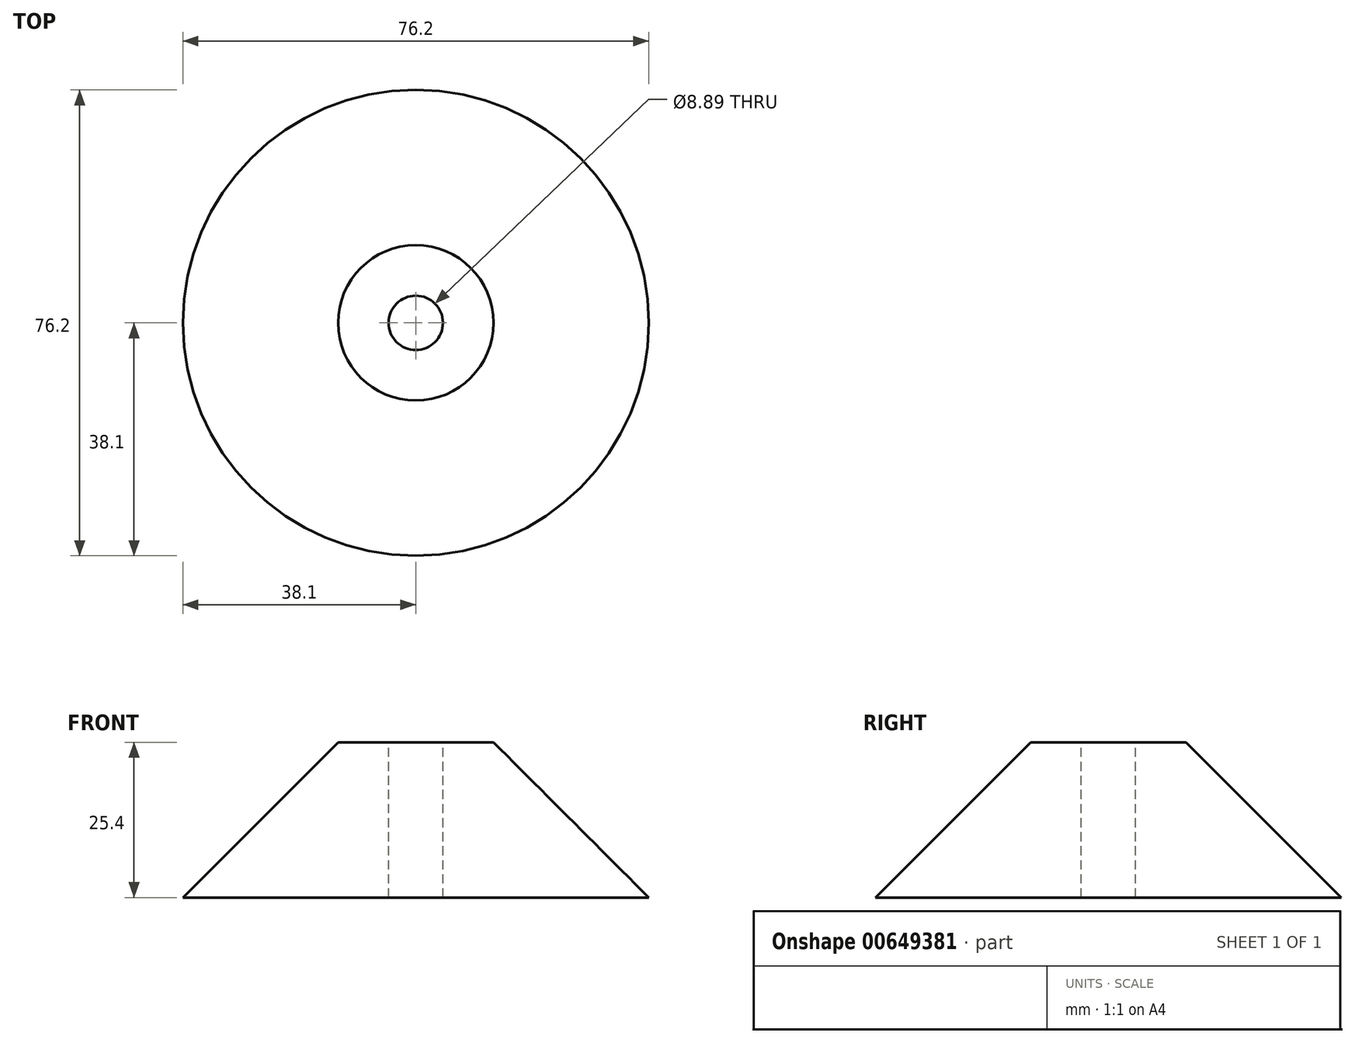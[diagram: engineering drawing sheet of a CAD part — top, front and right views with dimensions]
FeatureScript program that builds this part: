
annotation { "Feature Type Name" : "Feature", "Feature Type Description" : "" }
export const myFeature = defineFeature(function(context is Context, id is Id, definition is map)
    precondition{}
    {
        {
            var Q0;
            Q0=qCreatedBy(makeId("Top.planeOp"),FACE);
            var sketch = newSketch(context, id + "F0", { "sketchPlane" : qUnion([Q0])});
            skCircle(sketch, "E0", {"center": v(0, 0) * mm, "radius": 38.1 * mm});
            skSolve(sketch);
        }
        {
            var Q0;
            Q0=qCreatedBy(makeId("Top.planeOp"),FACE);
            cPlane(context, id + "F1", {"entities" : qUnion([Q0]), "cplaneType" : CPlaneType.OFFSET, "offset" : 25.4 * mm, "width" : 152.4 * mm, "height" : 152.4 * mm});
        }
        {
            var Q0;
            Q0=qCreatedBy(id+"F1.planeOp",FACE);
            var sketch = newSketch(context, id + "F2", { "sketchPlane" : qUnion([Q0])});
            skCircle(sketch, "E1", {"center": v(0, 0) * mm, "radius": 12.7 * mm});
            skSolve(sketch);
        }
        {
            var Q0;
            Q0=makeQuery(id+"F0.imprint","IMPRINT",FACE,{"disambiguationData":[TD([[makeQuery(id+"F0.imprint","IMPRINT",EDGE,{"derivedFrom":sQuery(id+"F0.wireOp",EDGE,"E0")}),1.0]])]});
            var Q1;
            Q1=makeQuery(id+"F2.imprint","IMPRINT",FACE,{"disambiguationData":[TD([[makeQuery(id+"F2.imprint","IMPRINT",EDGE,{"derivedFrom":sQuery(id+"F2.wireOp",EDGE,"E1")}),1.0]])]});
            var Q2;
            Q2=sQuery(id+"F2.wireOp",EDGE,"E1");
            loft(context, id + "F3", {"startCondition" : LoftEndDerivativeType.NORMAL_TO_PROFILE, "startMagnitude" : 0, "sheetProfilesArray" : [{ "sheetProfileEntities" : qUnion([Q0]) }, { "sheetProfileEntities" : qUnion([Q1]) }], "guidesArray" : [{ "guideEntities" : qUnion([Q2]), "guideDerivativeType" : LoftGuideDerivativeType.DEFAULT, "guideDerivativeMagnitude" : 1 }]});
        }
        {
            var Q0;
            Q0=makeQuery(id+"F3.opLoft","CAP_FACE",FACE,{"disambiguationData":[OSD([makeQuery(id+"F2.imprint","IMPRINT",FACE,{"disambiguationData":[TD([[makeQuery(id+"F2.imprint","IMPRINT",EDGE,{"derivedFrom":sQuery(id+"F2.wireOp",EDGE,"E1")}),1.0]])]})])],"isStart":true});
            var sketch = newSketch(context, id + "F4", { "sketchPlane" : qUnion([Q0])});
            skPoint(sketch, "E2", {"position": v(0, 0) * mm});
            skSolve(sketch);
        }
        {
            var Q0;
            Q0=sQuery(id+"F4.wireOp",VERTEX,"E2");
            var Q1;
            Q1=makeQuery(id+"F3.opLoft","SWEPT_BODY",BODY,{"disambiguationData":[OSD([makeQuery(id+"F0.imprint","IMPRINT",FACE,{"disambiguationData":[TD([[makeQuery(id+"F0.imprint","IMPRINT",EDGE,{"derivedFrom":sQuery(id+"F0.wireOp",EDGE,"E0")}),1.0]])]}),makeQuery(id+"F2.imprint","IMPRINT",FACE,{"disambiguationData":[TD([[makeQuery(id+"F2.imprint","IMPRINT",EDGE,{"derivedFrom":sQuery(id+"F2.wireOp",EDGE,"E1")}),1.0]])]})])]});
            hole(context, id + "F5", {"style" : HoleStyle.SIMPLE, "endStyle" : HoleEndStyle.THROUGH, "holeDiameter" : 8.9 * mm, "majorDiameter" : 6.35 * mm, "isTappedThrough" : true, "tappedDepth" : 12.7 * mm, "tapClearance" : 3, "locations" : qUnion([Q0]), "scope" : qUnion([Q1])});
        }
    });
